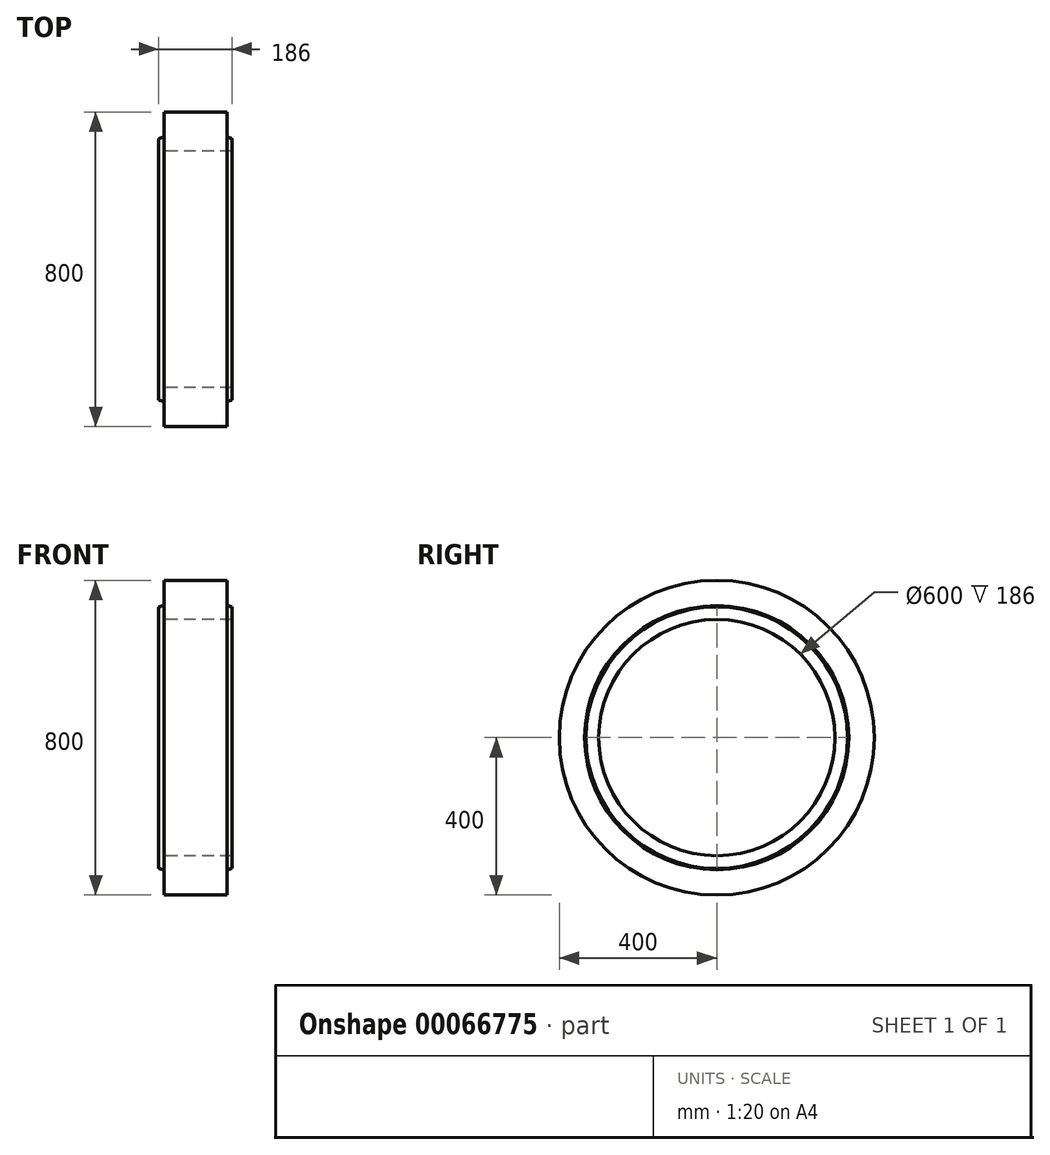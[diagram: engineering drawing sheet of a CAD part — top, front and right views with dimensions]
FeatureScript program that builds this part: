
annotation { "Feature Type Name" : "Feature", "Feature Type Description" : "" }
export const myFeature = defineFeature(function(context is Context, id is Id, definition is map)
    precondition{}
    {
        {
            var Q0;
            Q0=qCreatedBy(makeId("Front.planeOp"),FACE);
            var sketch = newSketch(context, id + "F0", { "sketchPlane" : qUnion([Q0])});
            skLineSegment(sketch, "E0", {"start": v(-80, 400) * mm, "end": v(80, 400) * mm});
            skLineSegment(sketch, "E1", {"start": v(-80, 400) * mm, "end": v(-80, 335.6) * mm});
            skLineSegment(sketch, "E2", {"start": v(80, 400) * mm, "end": v(80, 335.6) * mm});
            skArc(sketch, "E3", {"start": v(93, 332.23) * mm, "mid": v(0, 345) * mm, "end": v(-93, 332.23) * mm, "construction": true});
            skLineSegment(sketch, "E4", {"start": v(-93, 332.23) * mm, "end": v(-93, 300) * mm});
            skLineSegment(sketch, "E5", {"start": v(-93, 300) * mm, "end": v(93, 300) * mm});
            skLineSegment(sketch, "E6", {"start": v(93, 300) * mm, "end": v(93, 332.23) * mm});
            skLineSegment(sketch, "E7", {"start": v(0, 0) * mm, "end": v(348.72, 0) * mm, "construction": true});
            skArc(sketch, "E8", {"start": v(93, 332.23) * mm, "mid": v(86.52, 333.98) * mm, "end": v(80, 335.6) * mm});
            skArc(sketch, "E9", {"start": v(-80, 335.6) * mm, "mid": v(-86.52, 333.98) * mm, "end": v(-93, 332.23) * mm});
            skSolve(sketch);
        }
        {
            var Q0;
            Q0=makeQuery(id+"F0.imprint","IMPRINT",FACE,{"disambiguationData":[TD([[makeQuery(id+"F0.imprint","IMPRINT",EDGE,{"derivedFrom":sQuery(id+"F0.wireOp",EDGE,"E0")}),-1.0]])]});
            var Q1;
            Q1=sQuery(id+"F0.wireOp",EDGE,"E7");
            revolve(context, id + "F1", {"entities" : qUnion([Q0]), "axis" : qUnion([Q1]), "revolveType" : RevolveType.FULL});
        }
    });
